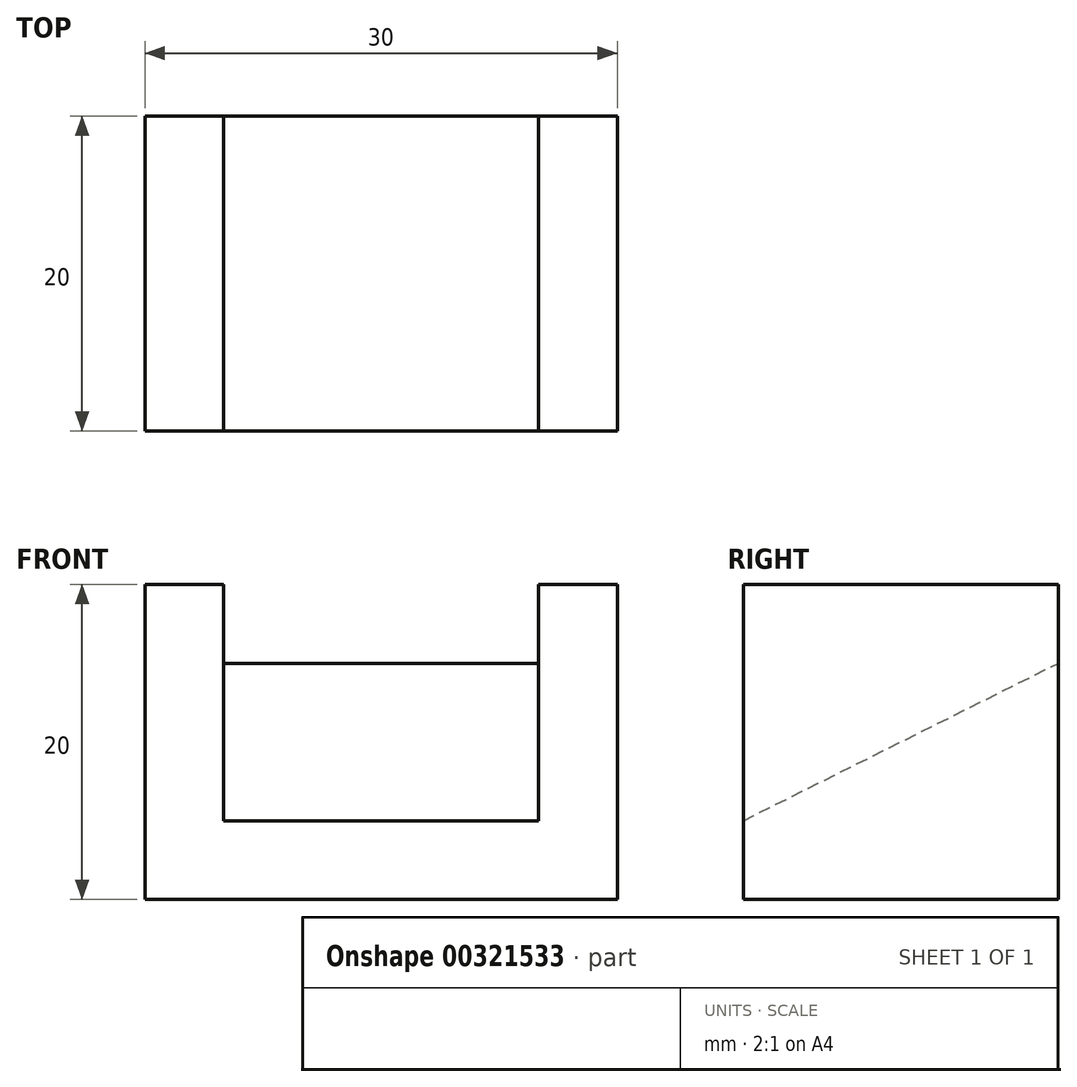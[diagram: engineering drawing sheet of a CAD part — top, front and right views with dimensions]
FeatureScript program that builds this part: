
annotation { "Feature Type Name" : "Feature", "Feature Type Description" : "" }
export const myFeature = defineFeature(function(context is Context, id is Id, definition is map)
    precondition{}
    {
        {
            var Q0;
            Q0=qCreatedBy(makeId("Right.planeOp"),FACE);
            var sketch = newSketch(context, id + "F0", { "sketchPlane" : qUnion([Q0])});
            skLineSegment(sketch, "E0", {"start": v(0, 0) * mm, "end": v(0, 20) * mm});
            skLineSegment(sketch, "E1", {"start": v(0, 20) * mm, "end": v(20, 20) * mm});
            skLineSegment(sketch, "E2", {"start": v(20, 20) * mm, "end": v(20, 0) * mm});
            skLineSegment(sketch, "E3", {"start": v(20, 0) * mm, "end": v(0, 0) * mm});
            skLineSegment(sketch, "E4", {"start": v(0, 5) * mm, "end": v(20, 15) * mm});
            skSolve(sketch);
        }
        {
            var Q0;
            {var subQ0=sQuery(id+"F0.wireOp",EDGE,"E1");Q0=makeQuery(id+"F0.imprint","IMPRINT",FACE,{"disambiguationData":[TD([[makeQuery(id+"F0.imprint","IMPRINT",EDGE,{"derivedFrom":subQ0}),-1.0]])]});}
            extrude(context, id + "F1", {"entities" : qUnion([Q0]), "depth" : 5 * mm});
        }
        {
            var Q0;
            {var subQ0=sQuery(id+"F0.wireOp",EDGE,"E3");Q0=makeQuery(id+"F0.imprint","IMPRINT",FACE,{"disambiguationData":[TD([[makeQuery(id+"F0.imprint","IMPRINT",EDGE,{"derivedFrom":subQ0}),-1.0]])]});}
            extrude(context, id + "F2", {"entities" : qUnion([Q0]), "operationType" : NewBodyOperationType.ADD, "depth" : 25 * mm});
        }
        {
            var Q0;
            Q0=makeQuery(id+"F2.opExtrude","CAP_FACE",FACE,{"disambiguationData":[OSD([sQuery(id+"F0.wireOp",EDGE,"E0"),sQuery(id+"F0.wireOp",EDGE,"E2"),sQuery(id+"F0.wireOp",EDGE,"E3"),sQuery(id+"F0.wireOp",EDGE,"E4")])],"isStart":false});
            var sketch = newSketch(context, id + "F3", { "sketchPlane" : qUnion([Q0])});
            skLineSegment(sketch, "E5.bottom", {"start": v(0, 0) * mm, "end": v(20, 0) * mm});
            skLineSegment(sketch, "E5.top", {"start": v(0, 20) * mm, "end": v(20, 20) * mm});
            skLineSegment(sketch, "E5.left", {"start": v(0, 0) * mm, "end": v(0, 20) * mm});
            skLineSegment(sketch, "E5.right", {"start": v(20, 0) * mm, "end": v(20, 20) * mm});
            skSolve(sketch);
        }
        {
            var Q0;
            Q0 = qSketchRegion(id + "F3", true);
            extrude(context, id + "F4", {"entities" : qUnion([Q0]), "operationType" : NewBodyOperationType.ADD, "depth" : 5 * mm});
        }
    });
